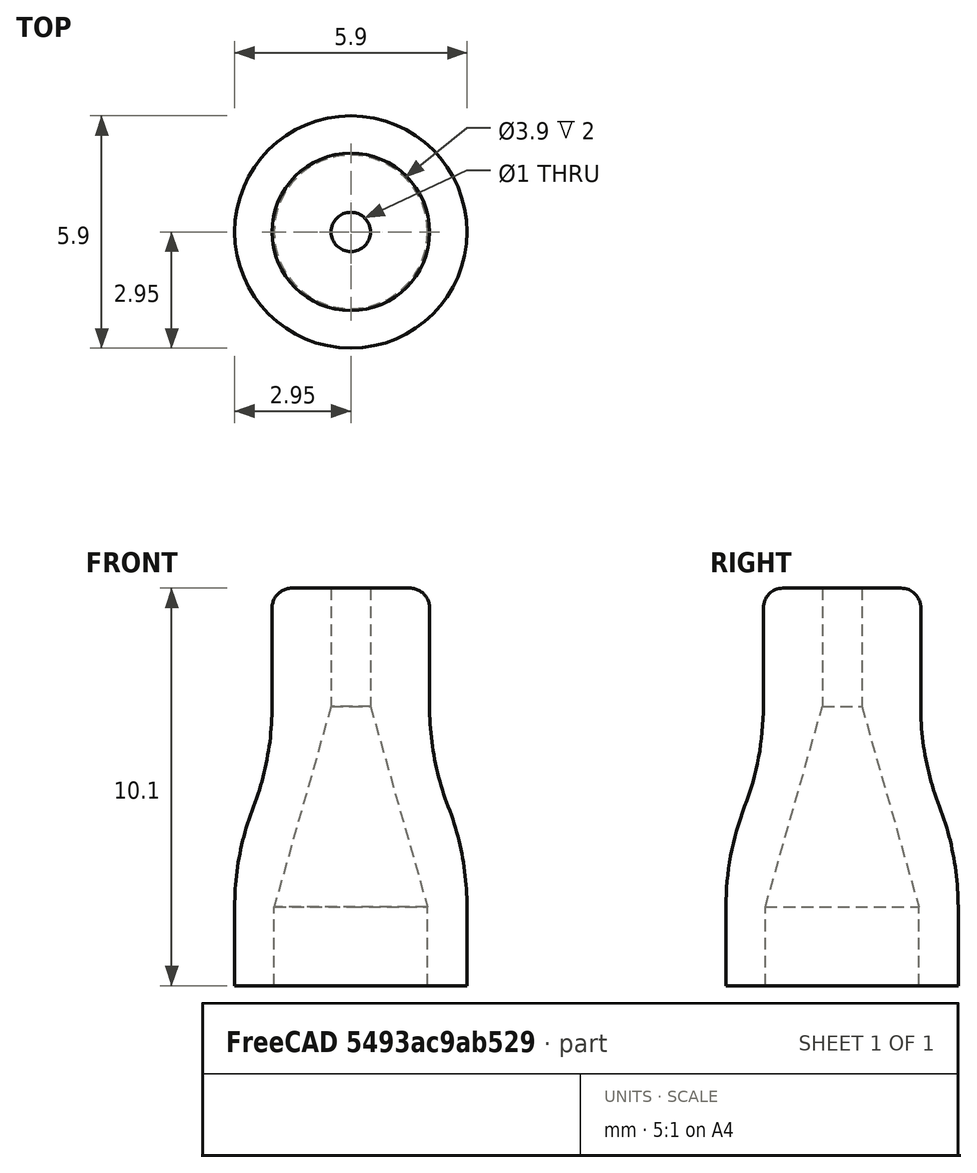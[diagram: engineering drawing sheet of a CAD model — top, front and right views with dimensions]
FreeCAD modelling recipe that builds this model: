
FCSTD DOCUMENT  (FreeCAD 0.18R16093 (Git))
Label: MagnetHolderRound
License: All rights reserved
LicenseURL: http://en.wikipedia.org/wiki/All_rights_reserved
objects: Sketcher::SketchObject×1, PartDesign::Revolution×1, PartDesign::Body×1
note: 4 computed .brp shape members not serialized (recipe doc carries the construction recipe); baked Part::Feature solids carry a one-line shape summary decoded from their .brp

FEATURE [Sketcher::SketchObject] Sketch
  MapMode = 5
  Placement = pos=(0,0,0) rot=(0.57735,0.57735,0.57735;2.0944rad)
  Support = -> [YZ_Plane]
  sketch-geometry (13):
    g0: LineSegment [constr] StartX=-1.95 StartY=-2 StartZ=0 EndX=0 EndY=-2 EndZ=0
    g1: LineSegment StartX=-1.95 StartY=-2 StartZ=0 EndX=-1.95 EndY=0 EndZ=0
    g2: LineSegment StartX=-0.5 StartY=8.1 StartZ=0 EndX=-0.5 EndY=5.1 EndZ=0
    g3: LineSegment StartX=-1.95 StartY=0 StartZ=0 EndX=-0.5 EndY=5.1 EndZ=0
    g4: LineSegment [constr] StartX=-0.5 StartY=8.1 StartZ=0 EndX=0 EndY=8.1 EndZ=0
    g5: LineSegment StartX=-0.5 StartY=8.1 StartZ=0 EndX=-1.5 EndY=8.1 EndZ=0
    g6: LineSegment StartX=-1.95 StartY=-2 StartZ=0 EndX=-2.95 EndY=-2 EndZ=0
    g7: LineSegment StartX=-2.95 StartY=-2 StartZ=0 EndX=-2.95 EndY=-1.3e-15 EndZ=0
    g8: LineSegment StartX=-2 StartY=7.6 StartZ=0 EndX=-2 EndY=5.1 EndZ=0
    g9: ArcOfCircle CenterX=4.13224 CenterY=8e-16 CenterZ=0 NormalX=0 NormalY=0 NormalZ=1 AngleXU=0 Radius=7.08224 StartAngle=2.77327 EndAngle=3.14159
    g10: ArcOfCircle CenterX=-9.08224 CenterY=5.1 CenterZ=0 NormalX=0 NormalY=0 NormalZ=1 AngleXU=0 Radius=7.08224 StartAngle=5.91486 EndAngle=6.28319
    g11: LineSegment [constr] StartX=-2 StartY=5.1 StartZ=0 EndX=-0.5 EndY=5.1 EndZ=0
    g12: ArcOfCircle CenterX=-1.5 CenterY=7.6 CenterZ=0 NormalX=0 NormalY=0 NormalZ=1 AngleXU=0 Radius=0.5 StartAngle=1.5708 EndAngle=3.14159
  constraints (36):
    c: Horizontal(g0)
    c: Coincident(g1,g0)
    c: PointOnObject(g1,g-1)
    c: Vertical(g1)
    c: PointOnObject(g0,g-2)
    c: Vertical(g2)
    c: Coincident(g3,g1)
    c: Coincident(g3,g2)
    c: Coincident(g4,g2)
    c: PointOnObject(g4,g-2)
    c: Horizontal(g4)
    c: DistanceX(g0,g0) = 1.95
    c: DistanceY(g0,g1) = 2
    c: DistanceX(g2,g4) = 0.5
    c: DistanceY(g2,g2) = 3
    c: DistanceY(g-1,g4) = 8.1
    c: Coincident(g5,g2)
    c: Horizontal(g5)
    c: Coincident(g6,g1)
    c: Horizontal(g6)
    c: Vertical(g7)
    c: Vertical(g8)
    c: Tangent(g9,g7) = 1.5708
    c: Tangent(g10,g8) = 1.5708
    c: Equal(g10,g9)
    c: PointOnObject(g7,g-1)
    c: Coincident(g11,g8)
    c: Coincident(g11,g2)
    c: Horizontal(g11)
    c: Tangent(g8,g12) = -1.5708
    c: Tangent(g5,g12) = -1.5708
    c: Radius(g12) = 0.5
    c: DistanceX(g8,g2) = 1.5
    c: DistanceX(g7,g1) = 1
    c: Tangent(g9,g10) = 1.5708
    c: Coincident(g7,g6)
FEATURE [PartDesign::Revolution] Revolution
  Angle = 360
  Axis = (-2e-16,3e-16,1)
  Base = (0,0,0)
  Placement = pos=(0,0,0) rot=(0.57735,0.57735,0.57735;2.0944rad)
  Profile = -> Sketch
  ReferenceAxis = -> Sketch [V_Axis]
FEATURE [PartDesign::Body] Body
  Group = -> [Sketch,Revolution]
  Origin = -> Origin
  Tip = -> Revolution
